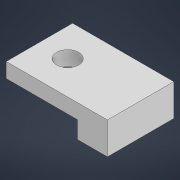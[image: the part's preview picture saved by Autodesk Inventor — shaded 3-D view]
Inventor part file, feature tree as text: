
AUTODESK INVENTOR PART (.ipt)
format: ipt  version: 2022 (Build 260153000, 153)  size: 113,152 bytes
history: native  units: mm
features: sketch x4, extrude x3
ambient origin geometry x8: Origin, YZ Plane, XZ Plane, XY Plane, X Axis, Y Axis, Z Axis, Center Point
bodies: Solid1 (feature_tree)
feature tree (7):
  extrude  "Extrusion1"  Depth=13.5mm
  extrude  "Extrusion2"  Depth=3.0mm
  extrude  "Extrusion3"  TaperAngle=0.0deg  [1 undecoded]
  sketch  "Sketch4"  dims[d7=0.0mm d8=14.5mm d9=0.0mm d10=4.5mm d11=5.75mm d12=6.75mm d13=14.5mm d14=0.0mm]
  sketch  "Sketch1"  dims[d0=6.5mm d1=13.5mm]
  sketch  "Sketch2"  dims[d2=6.1mm d3=0.0mm d4=3.0mm]
  sketch  "Sketch3"  dims[d5=13.5mm d6=0.0mm]
note: 1 required parameter value undecoded (feature->parameter linkage not recoverable at this tier; creation-order binding heuristic only, values carry confidence <= 0.55)
